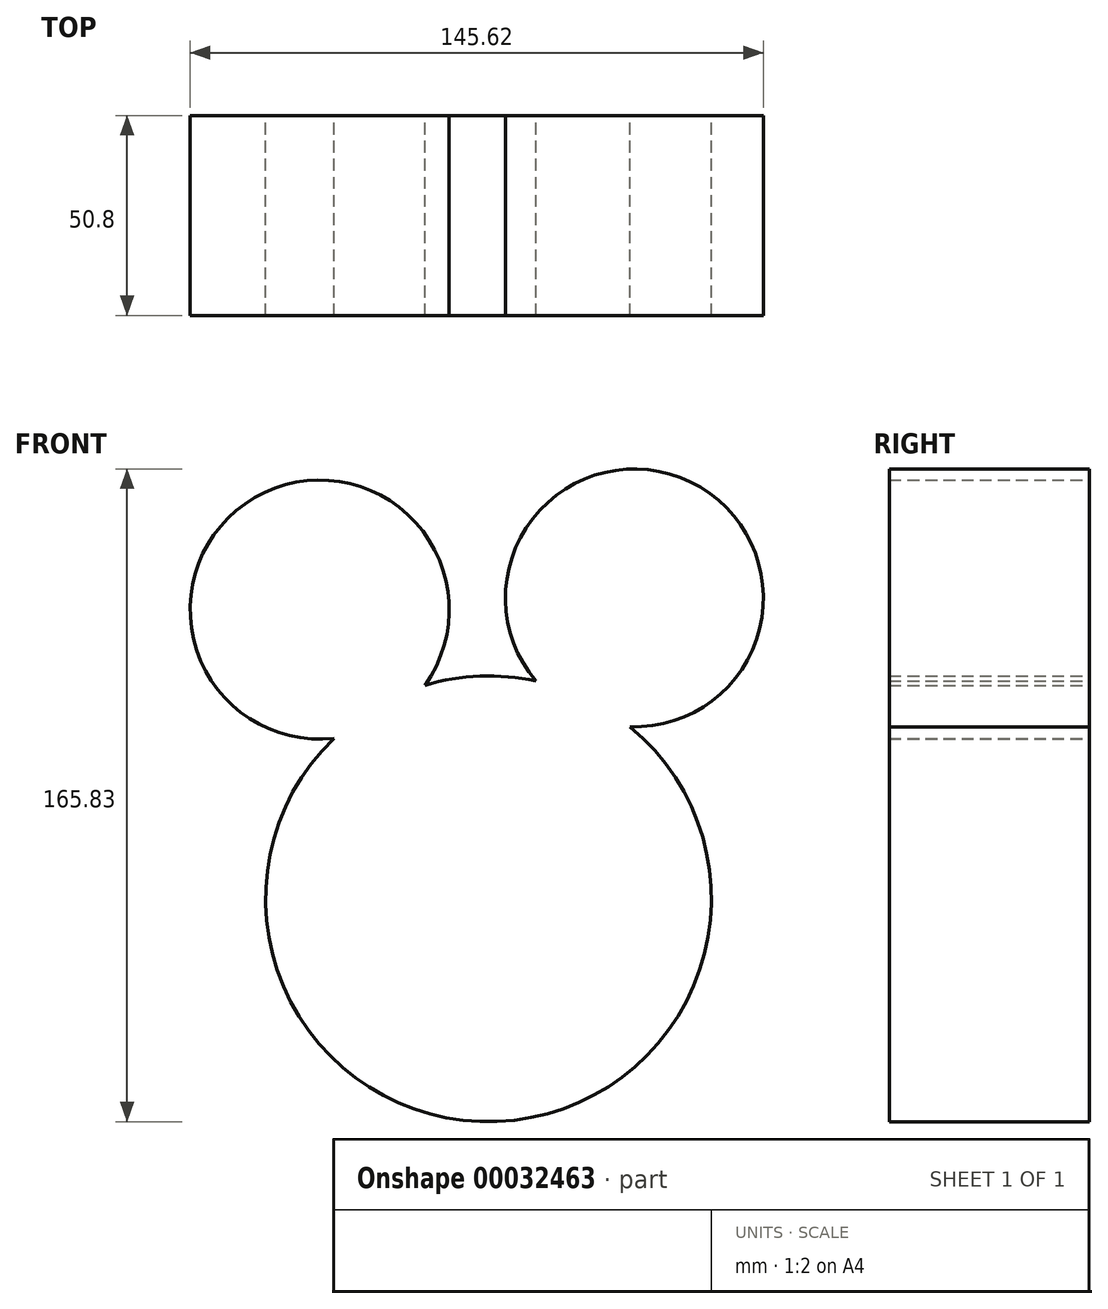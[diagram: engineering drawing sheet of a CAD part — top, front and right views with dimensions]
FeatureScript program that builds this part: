
annotation { "Feature Type Name" : "Feature", "Feature Type Description" : "" }
export const myFeature = defineFeature(function(context is Context, id is Id, definition is map)
    precondition{}
    {
        {
            var Q0;
            Q0=qCreatedBy(makeId("Front.planeOp"),FACE);
            var sketch = newSketch(context, id + "F0", { "sketchPlane" : qUnion([Q0])});
            skArc(sketch, "E0", {"start": v(-64.68, 14.42) * mm, "mid": v(-106.68, 64.6) * mm, "end": v(-76.52, 6.53) * mm});
            skArc(sketch, "E1", {"start": v(-10.02, 7.44) * mm, "mid": v(0.94, 71.55) * mm, "end": v(-25.2, 12) * mm});
            skCircle(sketch, "E2", {"center": v(-45.55, -36.29) * mm, "radius": 56.62 * mm});
            skSolve(sketch);
        }
        {
            var Q0;
            Q0=qCreatedBy(makeId("Front.planeOp"),FACE);
            var sketch = newSketch(context, id + "F1", { "sketchPlane" : qUnion([Q0])});
            skCircle(sketch, "E3", {"center": v(-75.12, -19.3) * mm, "radius": 10.8 * mm});
            skCircle(sketch, "E4", {"center": v(-25.93, -18.3) * mm, "radius": 10.02 * mm});
            skSolve(sketch);
        }
        {
            var Q0;
            Q0 = qSketchRegion(id + "F0", true);
            extrude(context, id + "F2", {"entities" : qUnion([Q0]), "depth" : 50.8 * mm});
        }
        {
            var Q0;
            Q0 = qSketchRegion(id + "F1", true);
            extrude(context, id + "F3", {"entities" : qUnion([Q0]), "operationType" : NewBodyOperationType.REMOVE, "oppositeDirection" : true, "depth" : 25.4 * mm});
        }
    });
